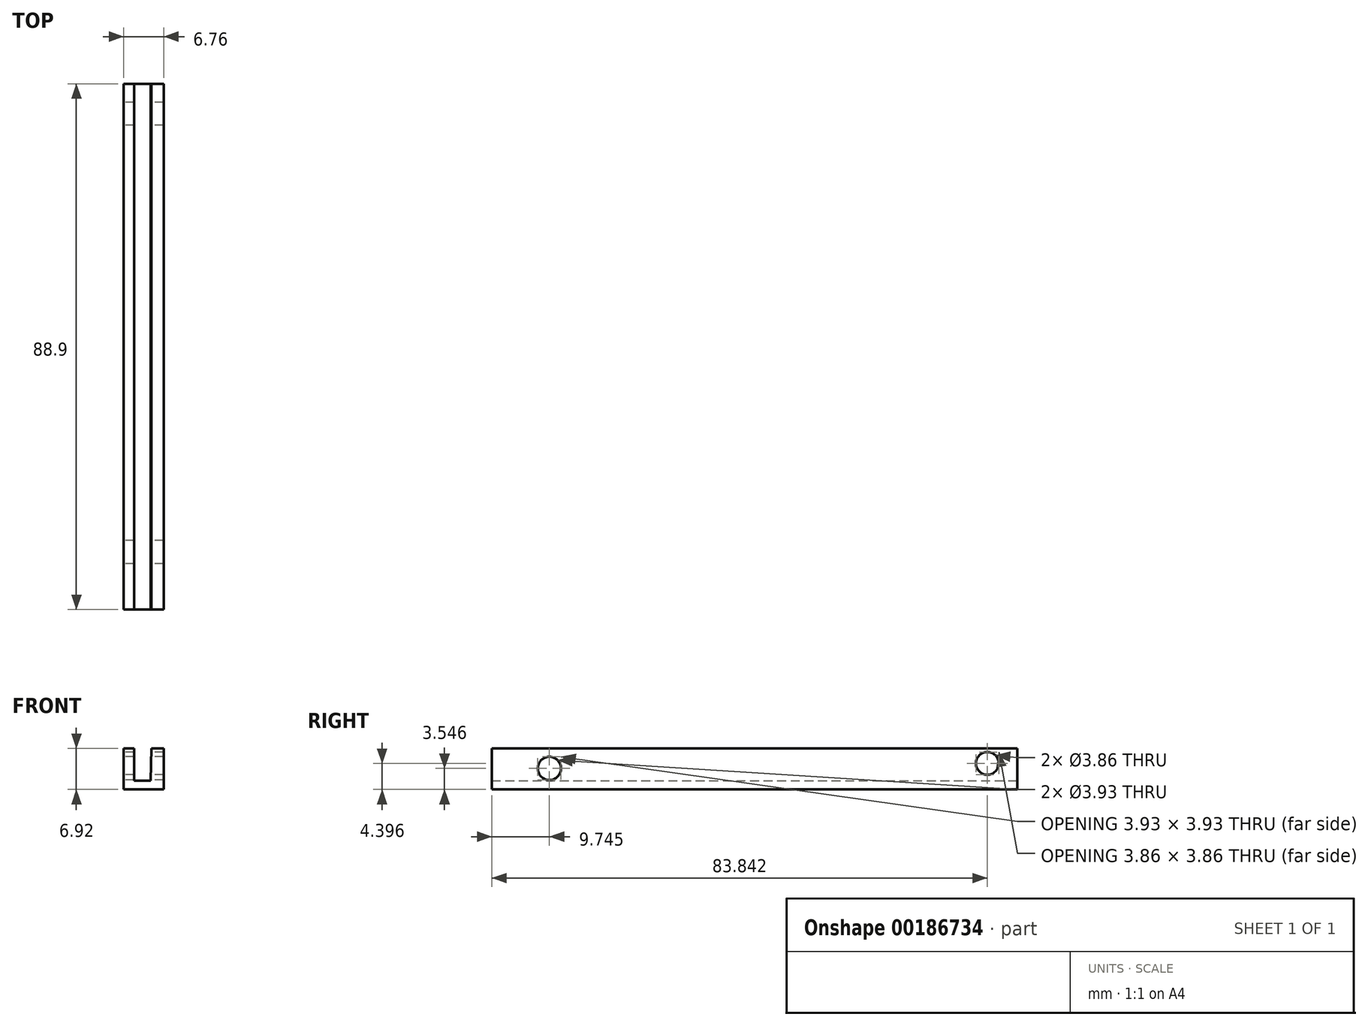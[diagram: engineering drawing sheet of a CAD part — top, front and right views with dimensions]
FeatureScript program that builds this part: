
annotation { "Feature Type Name" : "Feature", "Feature Type Description" : "" }
export const myFeature = defineFeature(function(context is Context, id is Id, definition is map)
    precondition{}
    {
        {
            var Q0;
            Q0=qCreatedBy(makeId("Front.planeOp"),FACE);
            var sketch = newSketch(context, id + "F0", { "sketchPlane" : qUnion([Q0])});
            skLineSegment(sketch, "E0", {"start": v(-39.55, 47.29) * mm, "end": v(-39.55, 40.37) * mm});
            skLineSegment(sketch, "E1", {"start": v(-39.55, 40.37) * mm, "end": v(-36.17, 40.37) * mm});
            skLineSegment(sketch, "E2.MirrorCS", {"start": v(-32.79, 47.29) * mm, "end": v(-32.79, 40.37) * mm});
            skLineSegment(sketch, "E3.MirrorCS", {"start": v(-32.79, 40.37) * mm, "end": v(-36.17, 40.37) * mm});
            skLineSegment(sketch, "E4", {"start": v(-39.55, 47.29) * mm, "end": v(-37.79, 47.29) * mm});
            skLineSegment(sketch, "E5", {"start": v(-34.85, 47.29) * mm, "end": v(-32.79, 47.29) * mm});
            skPoint(sketch, "E6.start.orphan", {"position": v(-36.17, 41.85) * mm});
            skLineSegment(sketch, "E7", {"start": v(-37.79, 47.29) * mm, "end": v(-37.79, 41.85) * mm});
            skLineSegment(sketch, "E8", {"start": v(-37.79, 41.85) * mm, "end": v(-35, 41.85) * mm});
            skLineSegment(sketch, "E9", {"start": v(-35, 41.85) * mm, "end": v(-34.85, 47.29) * mm});
            skSolve(sketch);
        }
        {
            var Q0;
            Q0 = qSketchRegion(id + "F0", true);
            extrude(context, id + "F1", {"entities" : qUnion([Q0]), "depth" : 88.9 * mm});
        }
        {
            var Q0;
            Q0=makeQuery(id+"F1.opExtrude","SWEPT_FACE",FACE,{"disambiguationData":[OSD([sQuery(id+"F0.wireOp",EDGE,"E0")])]});
            var sketch = newSketch(context, id + "F2", { "sketchPlane" : qUnion([Q0])});
            skCircle(sketch, "E10", {"center": v(5.06, 44.77) * mm, "radius": 1.93 * mm});
            skSolve(sketch);
        }
        {
            var Q0;
            Q0 = qSketchRegion(id + "F2", true);
            extrude(context, id + "F3", {"entities" : qUnion([Q0]), "operationType" : NewBodyOperationType.REMOVE, "oppositeDirection" : true, "depth" : 25.4 * mm});
        }
        {
            var Q0;
            Q0=makeQuery(id+"F1.opExtrude","SWEPT_FACE",FACE,{"disambiguationData":[OSD([sQuery(id+"F0.wireOp",EDGE,"E0")])]});
            var sketch = newSketch(context, id + "F4", { "sketchPlane" : qUnion([Q0])});
            skCircle(sketch, "E11", {"center": v(79.16, 43.92) * mm, "radius": 1.96 * mm});
            skSolve(sketch);
        }
        {
            var Q0;
            Q0 = qSketchRegion(id + "F4", true);
            extrude(context, id + "F5", {"entities" : qUnion([Q0]), "operationType" : NewBodyOperationType.REMOVE, "oppositeDirection" : true, "depth" : 25.4 * mm});
        }
    });
